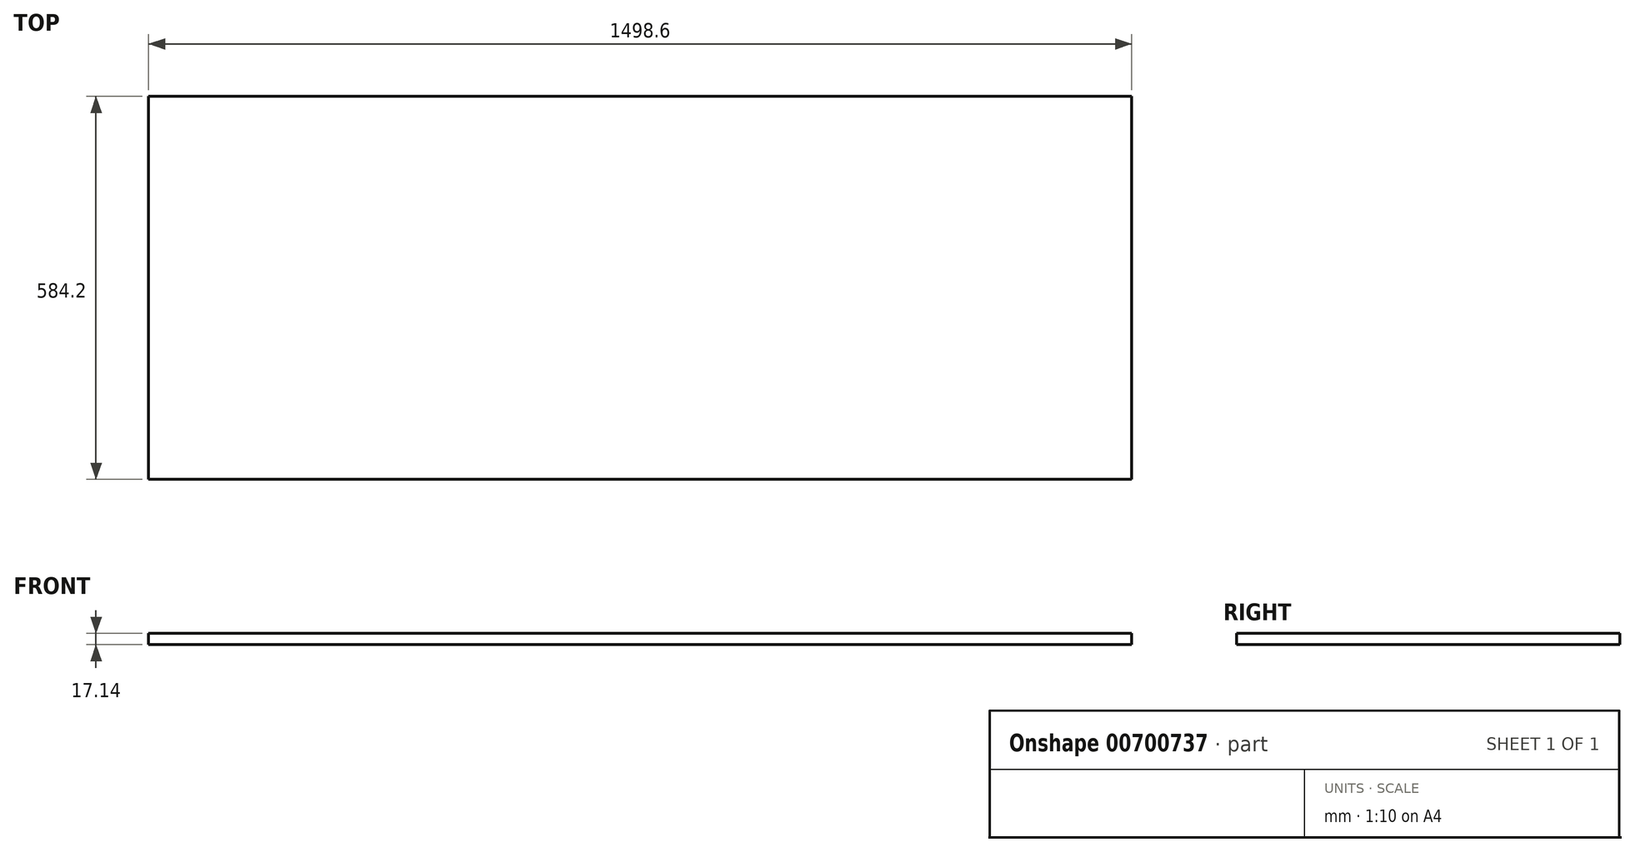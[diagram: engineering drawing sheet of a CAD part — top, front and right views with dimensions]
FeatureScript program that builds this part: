
annotation { "Feature Type Name" : "Feature", "Feature Type Description" : "" }
export const myFeature = defineFeature(function(context is Context, id is Id, definition is map)
    precondition{}
    {
        {
            var Q0;
            Q0=qCreatedBy(makeId("Top.planeOp"),FACE);
            var sketch = newSketch(context, id + "F0", { "sketchPlane" : qUnion([Q0])});
            skLineSegment(sketch, "E0.bottom", {"start": v(0, 0) * mm, "end": v(1498.6, 0) * mm});
            skLineSegment(sketch, "E0.top", {"start": v(0, 584.2) * mm, "end": v(1498.6, 584.2) * mm});
            skLineSegment(sketch, "E0.left", {"start": v(0, 0) * mm, "end": v(0, 584.2) * mm});
            skLineSegment(sketch, "E0.right", {"start": v(1498.6, 0) * mm, "end": v(1498.6, 584.2) * mm});
            skSolve(sketch);
        }
        {
            var Q0;
            Q0 = qSketchRegion(id + "F0", true);
            extrude(context, id + "F1", {"entities" : qUnion([Q0]), "depth" : 17.14 * mm, "offsetDistance" : 25.4 * mm});
        }
    });
